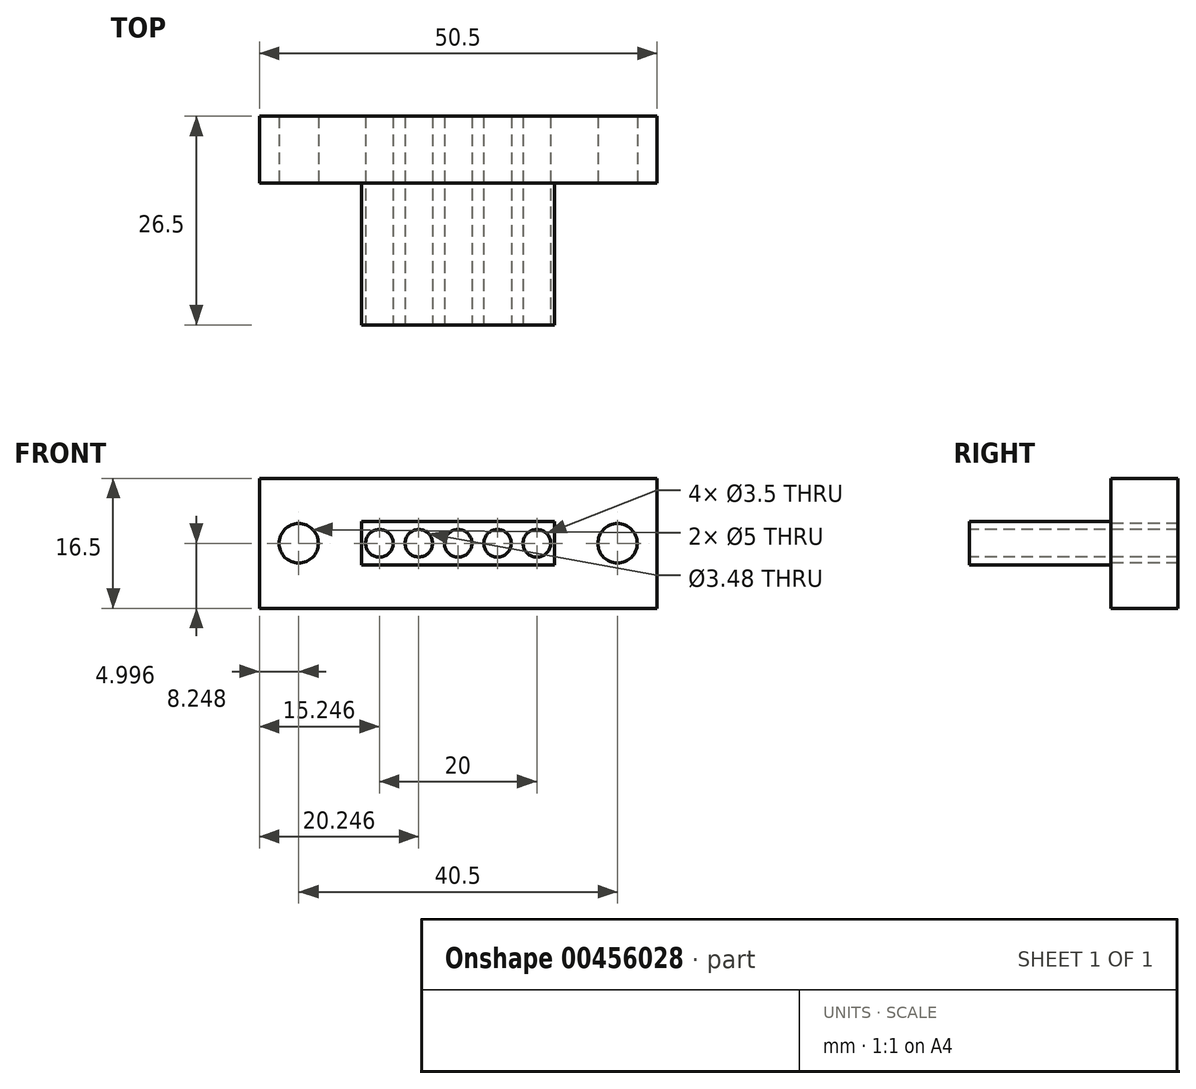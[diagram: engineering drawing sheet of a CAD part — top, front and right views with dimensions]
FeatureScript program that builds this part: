
annotation { "Feature Type Name" : "Feature", "Feature Type Description" : "" }
export const myFeature = defineFeature(function(context is Context, id is Id, definition is map)
    precondition{}
    {
        {
            var Q0;
            Q0=qCreatedBy(makeId("Front.planeOp"),FACE);
            var sketch = newSketch(context, id + "F0", { "sketchPlane" : qUnion([Q0])});
            skLineSegment(sketch, "E0.bottom", {"start": v(-26.01, 9.5) * mm, "end": v(24.49, 9.5) * mm});
            skLineSegment(sketch, "E0.top", {"start": v(-26.01, -7) * mm, "end": v(24.49, -7) * mm});
            skLineSegment(sketch, "E0.left", {"start": v(-26.01, 9.5) * mm, "end": v(-26.01, -7) * mm});
            skLineSegment(sketch, "E0.right", {"start": v(24.49, 9.5) * mm, "end": v(24.49, -7) * mm});
            skSolve(sketch);
        }
        {
            var Q0;
            Q0 = qSketchRegion(id + "F0", true);
            extrude(context, id + "F1", {"entities" : qUnion([Q0]), "depth" : 8.5 * mm});
        }
        {
            var Q0;
            Q0=makeQuery(id+"F1.opExtrude","CAP_FACE",FACE,{"disambiguationData":[OSD([sQuery(id+"F0.wireOp",EDGE,"E0.bottom"),sQuery(id+"F0.wireOp",EDGE,"E0.top"),sQuery(id+"F0.wireOp",EDGE,"E0.left"),sQuery(id+"F0.wireOp",EDGE,"E0.right")])],"isStart":false});
            var sketch = newSketch(context, id + "F2", { "sketchPlane" : qUnion([Q0])});
            skLineSegment(sketch, "E1.bottom", {"start": v(-13.01, 4) * mm, "end": v(11.49, 4) * mm});
            skLineSegment(sketch, "E1.top", {"start": v(-13.01, -1.5) * mm, "end": v(11.49, -1.5) * mm});
            skLineSegment(sketch, "E1.left", {"start": v(-13.01, 4) * mm, "end": v(-13.01, -1.5) * mm});
            skLineSegment(sketch, "E1.right", {"start": v(11.49, 4) * mm, "end": v(11.49, -1.5) * mm});
            skSolve(sketch);
        }
        {
            var Q0;
            Q0=makeQuery(id+"F2.imprint","IMPRINT",FACE,{"disambiguationData":[TD([[makeQuery(id+"F2.imprint","IMPRINT",EDGE,{"derivedFrom":sQuery(id+"F2.wireOp",EDGE,"E1.bottom")}),-1.0]])]});
            extrude(context, id + "F3", {"entities" : qUnion([Q0]), "operationType" : NewBodyOperationType.ADD, "depth" : 18 * mm});
        }
        {
            var Q0;
            Q0=makeQuery(id+"F3.opExtrude","CAP_FACE",FACE,{"disambiguationData":[OSD([sQuery(id+"F2.wireOp",EDGE,"E1.bottom"),sQuery(id+"F2.wireOp",EDGE,"E1.top"),sQuery(id+"F2.wireOp",EDGE,"E1.left"),sQuery(id+"F2.wireOp",EDGE,"E1.right")])],"isStart":false});
            var sketch = newSketch(context, id + "F4", { "sketchPlane" : qUnion([Q0])});
            skCircle(sketch, "E2", {"center": v(-10.76, 1.25) * mm, "radius": 1.75 * mm});
            skCircle(sketch, "E3", {"center": v(-5.76, 1.25) * mm, "radius": 1.74 * mm});
            skCircle(sketch, "E4", {"center": v(-0.76, 1.25) * mm, "radius": 1.75 * mm});
            skCircle(sketch, "E5", {"center": v(4.24, 1.25) * mm, "radius": 1.75 * mm});
            skCircle(sketch, "E6", {"center": v(9.24, 1.25) * mm, "radius": 1.75 * mm});
            skSolve(sketch);
        }
        {
            var Q0;
            Q0=makeQuery(id+"F4.imprint","IMPRINT",FACE,{"disambiguationData":[TD([[makeQuery(id+"F4.imprint","IMPRINT",EDGE,{"derivedFrom":sQuery(id+"F4.wireOp",EDGE,"E2")}),1.0]])]});
            var Q1;
            Q1=makeQuery(id+"F4.imprint","IMPRINT",FACE,{"disambiguationData":[TD([[makeQuery(id+"F4.imprint","IMPRINT",EDGE,{"derivedFrom":sQuery(id+"F4.wireOp",EDGE,"E3")}),1.0]])]});
            var Q2;
            Q2=makeQuery(id+"F4.imprint","IMPRINT",FACE,{"disambiguationData":[TD([[makeQuery(id+"F4.imprint","IMPRINT",EDGE,{"derivedFrom":sQuery(id+"F4.wireOp",EDGE,"E4")}),1.0]])]});
            var Q3;
            Q3=makeQuery(id+"F4.imprint","IMPRINT",FACE,{"disambiguationData":[TD([[makeQuery(id+"F4.imprint","IMPRINT",EDGE,{"derivedFrom":sQuery(id+"F4.wireOp",EDGE,"E5")}),1.0]])]});
            var Q4;
            Q4=makeQuery(id+"F4.imprint","IMPRINT",FACE,{"disambiguationData":[TD([[makeQuery(id+"F4.imprint","IMPRINT",EDGE,{"derivedFrom":sQuery(id+"F4.wireOp",EDGE,"E6")}),1.0]])]});
            extrude(context, id + "F5", {"entities" : qUnion([Q0, Q1, Q2, Q3, Q4]), "operationType" : NewBodyOperationType.REMOVE, "oppositeDirection" : true, "depth" : 31.5 * mm});
        }
        {
            var Q0;
            Q0=makeQuery(id+"F1.opExtrude","CAP_FACE",FACE,{"disambiguationData":[OSD([sQuery(id+"F0.wireOp",EDGE,"E0.bottom"),sQuery(id+"F0.wireOp",EDGE,"E0.top"),sQuery(id+"F0.wireOp",EDGE,"E0.left"),sQuery(id+"F0.wireOp",EDGE,"E0.right")])],"isStart":false});
            var sketch = newSketch(context, id + "F6", { "sketchPlane" : qUnion([Q0])});
            skCircle(sketch, "E7", {"center": v(-21.01, 1.25) * mm, "radius": 2.5 * mm});
            skCircle(sketch, "E8", {"center": v(19.49, 1.25) * mm, "radius": 2.5 * mm});
            skSolve(sketch);
        }
        {
            var Q0;
            Q0=makeQuery(id+"F6.imprint","IMPRINT",FACE,{"disambiguationData":[TD([[makeQuery(id+"F6.imprint","IMPRINT",EDGE,{"derivedFrom":sQuery(id+"F6.wireOp",EDGE,"E7")}),1.0]])]});
            var Q1;
            Q1=makeQuery(id+"F6.imprint","IMPRINT",FACE,{"disambiguationData":[TD([[makeQuery(id+"F6.imprint","IMPRINT",EDGE,{"derivedFrom":sQuery(id+"F6.wireOp",EDGE,"7lHp1DZt-gj02-XFs1-jdsR-DjuwXVbLfmZr")}),1.0]])]});
            extrude(context, id + "F7", {"entities" : qUnion([Q0, Q1]), "operationType" : NewBodyOperationType.REMOVE, "oppositeDirection" : true, "depth" : 8.5 * mm});
        }
        {
            var Q0;
            Q0 = qSketchRegion(id + "F6", true);
            extrude(context, id + "F8", {"entities" : qUnion([Q0]), "operationType" : NewBodyOperationType.REMOVE, "oppositeDirection" : true, "depth" : 25 * mm});
        }
    });
